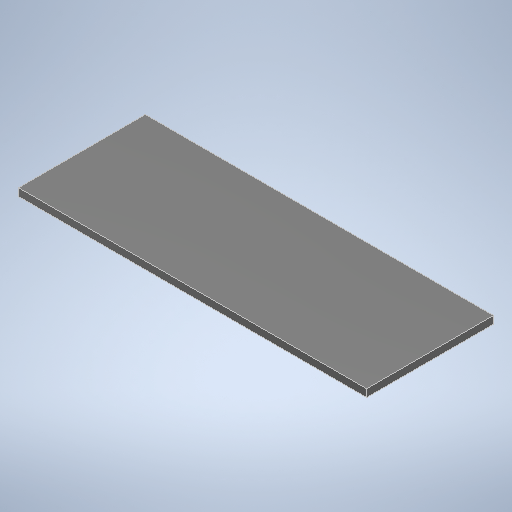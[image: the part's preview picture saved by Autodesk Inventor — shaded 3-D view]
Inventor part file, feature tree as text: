
AUTODESK INVENTOR PART (.ipt)
format: ipt  version: 2025 (Build 290162000, 162)  size: 242,176 bytes
history: native  units: mm
features: extrude x1, sketch x1
ambient origin geometry x8: Origin, YZ Plane, XZ Plane, XY Plane, X Axis, Y Axis, Z Axis, Center Point
bodies: Solid1 (feature_tree)
feature tree (2):
  extrude  "Extrusion1"  Depth=212.0mm
  sketch  "Sketch1"  dims[d0=582.0mm d1=212.0mm d2=12.7mm d3=0.0mm]
